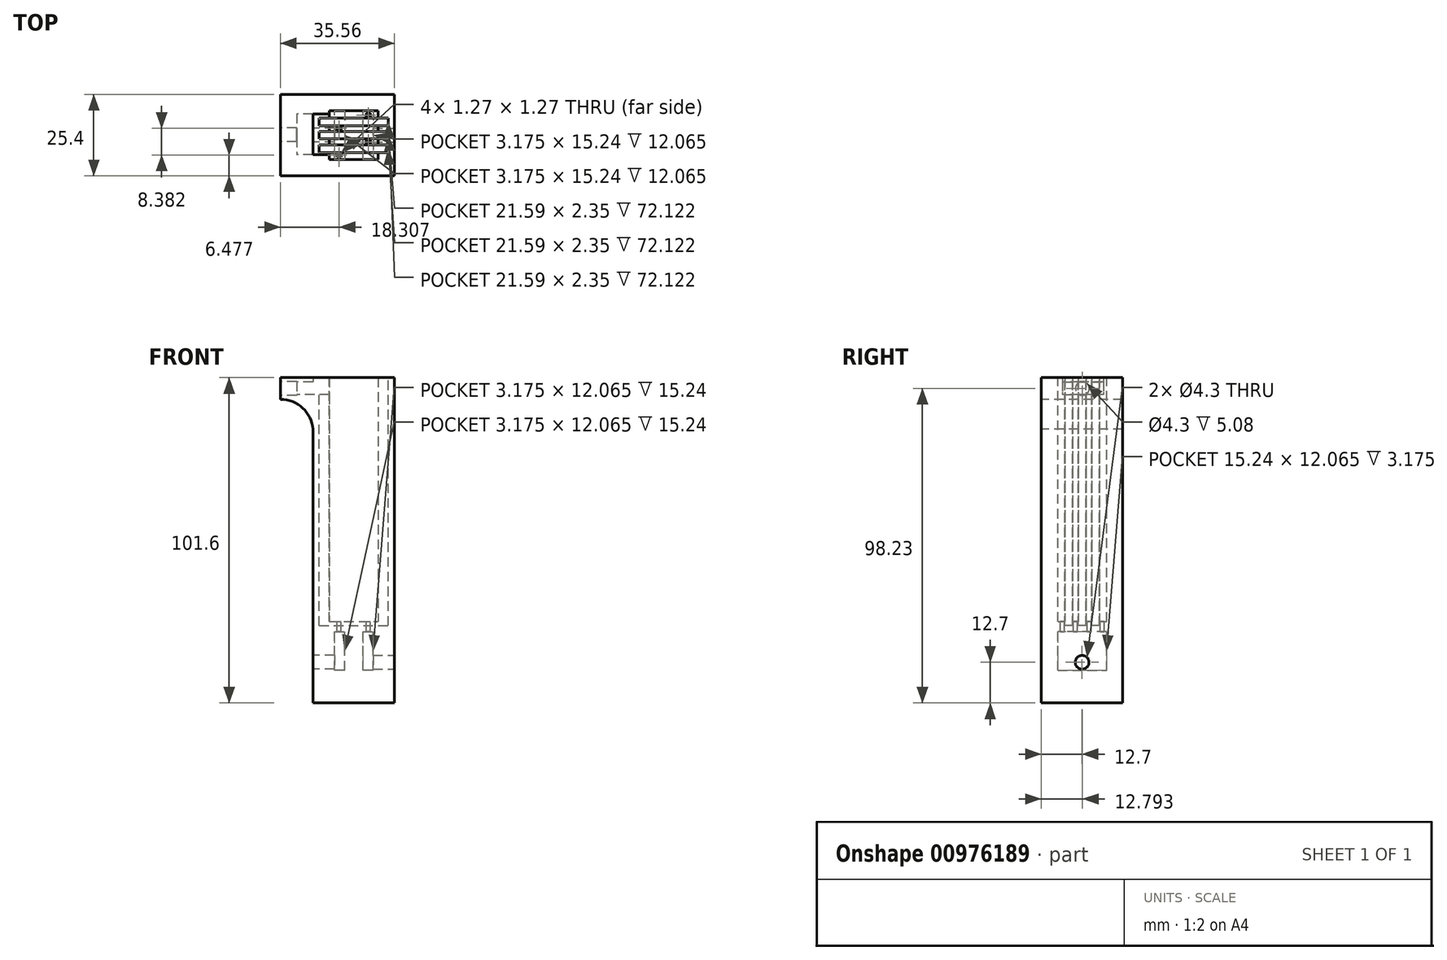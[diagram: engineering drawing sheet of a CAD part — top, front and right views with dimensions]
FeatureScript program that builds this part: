
annotation { "Feature Type Name" : "Feature", "Feature Type Description" : "" }
export const myFeature = defineFeature(function(context is Context, id is Id, definition is map)
    precondition{}
    {
        {
            var Q0;
            Q0=qCreatedBy(makeId("Top.planeOp"),FACE);
            var sketch = newSketch(context, id + "F0", { "sketchPlane" : qUnion([Q0])});
            skLineSegment(sketch, "E0.bottom", {"start": v(0, 0) * mm, "end": v(25.4, 0) * mm});
            skLineSegment(sketch, "E0.top", {"start": v(0, 25.4) * mm, "end": v(25.4, 25.4) * mm});
            skLineSegment(sketch, "E0.left", {"start": v(0, 0) * mm, "end": v(0, 25.4) * mm});
            skLineSegment(sketch, "E0.right", {"start": v(25.4, 0) * mm, "end": v(25.4, 25.4) * mm});
            skSolve(sketch);
        }
        {
            var Q0;
            Q0=makeQuery(id+"F0.imprint","IMPRINT",FACE,{"disambiguationData":[TD([[makeQuery(id+"F0.imprint","IMPRINT",EDGE,{"derivedFrom":sQuery(id+"F0.wireOp",EDGE,"E0.bottom")}),1.0]])]});
            extrude(context, id + "F1", {"entities" : qUnion([Q0]), "depth" : 101.6 * mm, "offsetDistance" : 25.4 * mm});
        }
        {
            var Q0;
            Q0=makeQuery(id+"F1.opExtrude","CAP_FACE",FACE,{"disambiguationData":[OSD([sQuery(id+"F0.wireOp",EDGE,"E0.bottom"),sQuery(id+"F0.wireOp",EDGE,"E0.top"),sQuery(id+"F0.wireOp",EDGE,"E0.left"),sQuery(id+"F0.wireOp",EDGE,"E0.right")])],"isStart":false});
            var sketch = newSketch(context, id + "F2", { "sketchPlane" : qUnion([Q0])});
            skLineSegment(sketch, "E1.bottom", {"start": v(5.08, 5.08) * mm, "end": v(20.32, 5.08) * mm});
            skLineSegment(sketch, "E1.top", {"start": v(5.08, 20.32) * mm, "end": v(20.32, 20.32) * mm});
            skLineSegment(sketch, "E1.left", {"start": v(5.08, 5.08) * mm, "end": v(5.08, 20.32) * mm});
            skLineSegment(sketch, "E1.right", {"start": v(20.32, 5.08) * mm, "end": v(20.32, 20.32) * mm});
            skSolve(sketch);
        }
        {
            var Q0;
            Q0=makeQuery(id+"F2.imprint","IMPRINT",FACE,{"disambiguationData":[TD([[makeQuery(id+"F2.imprint","IMPRINT",EDGE,{"derivedFrom":sQuery(id+"F2.wireOp",EDGE,"E1.bottom")}),1.0]])]});
            extrude(context, id + "F3", {"entities" : qUnion([Q0]), "operationType" : NewBodyOperationType.REMOVE, "oppositeDirection" : true, "depth" : 76.2 * mm, "offsetDistance" : 25.4 * mm});
        }
        {
            var Q0;
            Q0=makeQuery(id+"F1.opExtrude","SWEPT_FACE",FACE,{"disambiguationData":[OSD([sQuery(id+"F0.wireOp",EDGE,"E0.right")])]});
            var sketch = newSketch(context, id + "F4", { "sketchPlane" : qUnion([Q0])});
            skCircle(sketch, "E2", {"center": v(12.7, 12.7) * mm, "radius": 2.15 * mm});
            skSolve(sketch);
        }
        {
            var Q0;
            Q0=makeQuery(id+"F3.boolean.opBoolean","COPY",FACE,{"derivedFrom":makeQuery(id+"F3.opExtrude","CAP_FACE",FACE,{"disambiguationData":[OSD([sQuery(id+"F2.wireOp",EDGE,"E1.bottom"),sQuery(id+"F2.wireOp",EDGE,"E1.top"),sQuery(id+"F2.wireOp",EDGE,"E1.left"),sQuery(id+"F2.wireOp",EDGE,"E1.right")])],"isStart":false})});
            var sketch = newSketch(context, id + "F5", { "sketchPlane" : qUnion([Q0])});
            skLineSegment(sketch, "E3.bottom", {"start": v(15.56, 20.32) * mm, "end": v(18.73, 20.32) * mm});
            skLineSegment(sketch, "E3.top", {"start": v(15.56, 5.08) * mm, "end": v(18.73, 5.08) * mm});
            skLineSegment(sketch, "E3.left", {"start": v(15.56, 20.32) * mm, "end": v(15.56, 5.08) * mm});
            skLineSegment(sketch, "E3.right", {"start": v(18.73, 20.32) * mm, "end": v(18.73, 5.08) * mm});
            skLineSegment(sketch, "E4.bottom", {"start": v(6.67, 20.32) * mm, "end": v(9.84, 20.32) * mm});
            skLineSegment(sketch, "E4.top", {"start": v(6.67, 5.08) * mm, "end": v(9.84, 5.08) * mm});
            skLineSegment(sketch, "E4.left", {"start": v(6.67, 20.32) * mm, "end": v(6.67, 5.08) * mm});
            skLineSegment(sketch, "E4.right", {"start": v(9.84, 20.32) * mm, "end": v(9.84, 5.08) * mm});
            skSolve(sketch);
        }
        {
            var Q0;
            Q0=qSketchRegion(id+"F5",true);
            extrude(context, id + "F6", {"entities" : qUnion([Q0]), "operationType" : NewBodyOperationType.REMOVE, "endBound" : BoundingType.UP_TO_NEXT, "oppositeDirection" : true, "depth" : 25.4 * mm, "hasOffset" : true, "offsetDistance" : 10.16 * mm, "hasSecondDirection" : true, "secondDirectionOppositeDirection" : false, "secondDirectionDepth" : -3.17 * mm});
        }
        {
            var Q0;
            Q0=qSketchRegion(id+"F4",true);
            extrude(context, id + "F7", {"entities" : qUnion([Q0]), "operationType" : NewBodyOperationType.REMOVE, "endBound" : BoundingType.UP_TO_NEXT, "oppositeDirection" : true, "depth" : 25.4 * mm, "offsetDistance" : 25.4 * mm});
        }
        {
            var Q0;
            Q0=makeQuery(id+"F1.opExtrude","SWEPT_FACE",FACE,{"disambiguationData":[OSD([sQuery(id+"F0.wireOp",EDGE,"E0.left")])]});
            var sketch = newSketch(context, id + "F8", { "sketchPlane" : qUnion([Q0])});
            skCircle(sketch, "E5", {"center": v(-12.7, 12.7) * mm, "radius": 2.15 * mm});
            skSolve(sketch);
        }
        {
            var Q0;
            Q0=qSketchRegion(id+"F8",true);
            extrude(context, id + "F9", {"entities" : qUnion([Q0]), "operationType" : NewBodyOperationType.REMOVE, "endBound" : BoundingType.UP_TO_NEXT, "oppositeDirection" : true, "depth" : 25.4 * mm, "offsetDistance" : 25.4 * mm});
        }
        {
            var Q0;
            Q0=makeQuery(id+"F3.boolean.opBoolean","COPY",FACE,{"derivedFrom":makeQuery(id+"F3.opExtrude","CAP_FACE",FACE,{"disambiguationData":[OSD([sQuery(id+"F2.wireOp",EDGE,"E1.bottom"),sQuery(id+"F2.wireOp",EDGE,"E1.top"),sQuery(id+"F2.wireOp",EDGE,"E1.left"),sQuery(id+"F2.wireOp",EDGE,"E1.right")])],"isStart":false})});
            var sketch = newSketch(context, id + "F10", { "sketchPlane" : qUnion([Q0])});
            skLineSegment(sketch, "E6.bottom", {"start": v(16.57, 19.56) * mm, "end": v(17.84, 19.56) * mm});
            skLineSegment(sketch, "E6.top", {"start": v(16.57, 18.29) * mm, "end": v(17.84, 18.29) * mm});
            skLineSegment(sketch, "E6.left", {"start": v(16.57, 19.56) * mm, "end": v(16.57, 18.29) * mm});
            skLineSegment(sketch, "E6.right", {"start": v(17.84, 19.56) * mm, "end": v(17.84, 18.29) * mm});
            skLineSegment(sketch, "E7.0.1.0", {"start": v(16.57, 11.18) * mm, "end": v(17.84, 11.18) * mm});
            skLineSegment(sketch, "E7.0.1.1", {"start": v(17.84, 11.18) * mm, "end": v(17.84, 9.9) * mm});
            skLineSegment(sketch, "E7.0.1.2", {"start": v(16.57, 9.9) * mm, "end": v(17.84, 9.9) * mm});
            skLineSegment(sketch, "E7.0.1.3", {"start": v(16.57, 11.18) * mm, "end": v(16.57, 9.9) * mm});
            skLineSegment(sketch, "E7.direction1", {"start": v(16.57, 18.29) * mm, "end": v(41.97, 18.29) * mm, "construction": true});
            skLineSegment(sketch, "E7.direction2", {"start": v(16.57, 18.29) * mm, "end": v(16.57, 9.9) * mm, "construction": true});
            skSolve(sketch);
        }
        {
            var Q0;
            Q0=makeQuery(id+"F10.imprint","IMPRINT",FACE,{"disambiguationData":[TD([[makeQuery(id+"F10.imprint","IMPRINT",EDGE,{"derivedFrom":sQuery(id+"F10.wireOp",EDGE,"E6.bottom")}),1.0]])]});
            var sketch = newSketch(context, id + "F11", { "sketchPlane" : qUnion([Q0])});
            skLineSegment(sketch, "E8.bottom", {"start": v(7.51, 7.11) * mm, "end": v(8.78, 7.11) * mm});
            skLineSegment(sketch, "E8.top", {"start": v(7.51, 5.84) * mm, "end": v(8.78, 5.84) * mm});
            skLineSegment(sketch, "E8.left", {"start": v(7.51, 7.11) * mm, "end": v(7.51, 5.84) * mm});
            skLineSegment(sketch, "E8.right", {"start": v(8.78, 7.11) * mm, "end": v(8.78, 5.84) * mm});
            skLineSegment(sketch, "E9.bottom", {"start": v(7.51, 15.5) * mm, "end": v(8.78, 15.5) * mm});
            skLineSegment(sketch, "E9.top", {"start": v(7.51, 14.22) * mm, "end": v(8.78, 14.22) * mm});
            skLineSegment(sketch, "E9.left", {"start": v(7.51, 15.5) * mm, "end": v(7.51, 14.22) * mm});
            skLineSegment(sketch, "E9.right", {"start": v(8.78, 15.5) * mm, "end": v(8.78, 14.22) * mm});
            skSolve(sketch);
        }
        {
            var Q0;
            Q0=qSketchRegion(id+"F10",true);
            extrude(context, id + "F12", {"entities" : qUnion([Q0]), "operationType" : NewBodyOperationType.REMOVE, "endBound" : BoundingType.UP_TO_NEXT, "oppositeDirection" : true, "depth" : 25.4 * mm, "offsetDistance" : 25.4 * mm});
        }
        {
            var Q0;
            Q0=qSketchRegion(id+"F11",true);
            extrude(context, id + "F13", {"entities" : qUnion([Q0]), "operationType" : NewBodyOperationType.REMOVE, "endBound" : BoundingType.UP_TO_NEXT, "oppositeDirection" : true, "depth" : 25.4 * mm, "offsetDistance" : 25.4 * mm});
        }
        {
            var Q0;
            Q0=makeQuery(id+"F1.opExtrude","SWEPT_FACE",FACE,{"disambiguationData":[OSD([sQuery(id+"F0.wireOp",EDGE,"E0.left")])]});
            var sketch = newSketch(context, id + "F14", { "sketchPlane" : qUnion([Q0])});
            skLineSegment(sketch, "E10.bottom", {"start": v(-19.33, 100.27) * mm, "end": v(-6.55, 100.27) * mm});
            skLineSegment(sketch, "E10.top", {"start": v(-19.33, 96.25) * mm, "end": v(-6.55, 96.25) * mm});
            skLineSegment(sketch, "E10.left", {"start": v(-19.33, 100.27) * mm, "end": v(-19.33, 96.25) * mm});
            skLineSegment(sketch, "E10.right", {"start": v(-6.55, 100.27) * mm, "end": v(-6.55, 96.25) * mm});
            skSolve(sketch);
        }
        {
            var Q0;
            Q0=qSketchRegion(id+"F14",true);
            extrude(context, id + "F15", {"entities" : qUnion([Q0]), "operationType" : NewBodyOperationType.REMOVE, "endBound" : BoundingType.UP_TO_NEXT, "oppositeDirection" : true, "depth" : 25.4 * mm, "offsetDistance" : 25.4 * mm});
        }
        {
            var Q0;
            Q0=makeQuery(id+"F1.opExtrude","SWEPT_FACE",FACE,{"disambiguationData":[OSD([sQuery(id+"F0.wireOp",EDGE,"E0.left")])]});
            var sketch = newSketch(context, id + "F16", { "sketchPlane" : qUnion([Q0])});
            skLineSegment(sketch, "E11.bottom", {"start": v(-25.4, 101.6) * mm, "end": v(0, 101.6) * mm});
            skLineSegment(sketch, "E11.top", {"start": v(-25.4, 94.82) * mm, "end": v(0, 94.82) * mm});
            skLineSegment(sketch, "E11.left", {"start": v(-25.4, 101.6) * mm, "end": v(-25.4, 94.82) * mm});
            skLineSegment(sketch, "E11.right", {"start": v(0, 101.6) * mm, "end": v(0, 94.82) * mm});
            skSolve(sketch);
        }
        {
            var Q0;
            Q0=makeQuery(id+"F16.imprint","IMPRINT",FACE,{"disambiguationData":[TD([[makeQuery(id+"F16.imprint","IMPRINT",EDGE,{"derivedFrom":sQuery(id+"F16.wireOp",EDGE,"E11.bottom")}),1.0]])]});
            extrude(context, id + "F17", {"entities" : qUnion([Q0]), "operationType" : NewBodyOperationType.ADD, "depth" : 5.08 * mm, "offsetDistance" : 25.4 * mm});
        }
        {
            var Q0;
            Q0=makeQuery(id+"F17.opExtrude","CAP_FACE",FACE,{"disambiguationData":[OSD([sQuery(id+"F14.wireOp",EDGE,"E10.bottom"),sQuery(id+"F14.wireOp",EDGE,"E10.top"),sQuery(id+"F14.wireOp",EDGE,"E10.left"),sQuery(id+"F14.wireOp",EDGE,"E10.right"),sQuery(id+"F16.wireOp",EDGE,"E11.bottom"),sQuery(id+"F16.wireOp",EDGE,"E11.top"),sQuery(id+"F16.wireOp",EDGE,"E11.left"),sQuery(id+"F16.wireOp",EDGE,"E11.right")])],"isStart":false});
            var sketch = newSketch(context, id + "F18", { "sketchPlane" : qUnion([Q0])});
            skLineSegment(sketch, "E12.bottom", {"start": v(-25.4, 101.6) * mm, "end": v(0, 101.6) * mm});
            skLineSegment(sketch, "E12.top", {"start": v(-25.4, 94.82) * mm, "end": v(0, 94.82) * mm});
            skLineSegment(sketch, "E12.left", {"start": v(-25.4, 101.6) * mm, "end": v(-25.4, 94.82) * mm});
            skLineSegment(sketch, "E12.right", {"start": v(0, 101.6) * mm, "end": v(0, 94.82) * mm});
            skSolve(sketch);
        }
        {
            var Q0;
            Q0=qSketchRegion(id+"F18",true);
            extrude(context, id + "F19", {"entities" : qUnion([Q0]), "operationType" : NewBodyOperationType.ADD, "depth" : 5.08 * mm, "offsetDistance" : 25.4 * mm});
        }
        {
            var Q0;
            Q0=makeQuery(id+"F19.opExtrude","CAP_FACE",FACE,{"disambiguationData":[OSD([sQuery(id+"F18.wireOp",EDGE,"E12.bottom"),sQuery(id+"F18.wireOp",EDGE,"E12.top"),sQuery(id+"F18.wireOp",EDGE,"E12.left"),sQuery(id+"F18.wireOp",EDGE,"E12.right")])],"isStart":false});
            var sketch = newSketch(context, id + "F20", { "sketchPlane" : qUnion([Q0])});
            skCircle(sketch, "E13", {"center": v(-12.8, 98.23) * mm, "radius": 2.15 * mm});
            skSolve(sketch);
        }
        {
            var Q0;
            Q0=qSketchRegion(id+"F20",true);
            extrude(context, id + "F21", {"entities" : qUnion([Q0]), "operationType" : NewBodyOperationType.REMOVE, "oppositeDirection" : true, "depth" : 5.08 * mm, "offsetDistance" : 25.4 * mm});
        }
        {
            var Q0;
            Q0=makeQuery(id+"F19.boolean.opBoolean","MERGE",FACE,{"derivedFrom":[makeQuery(id+"F17.boolean.opBoolean","MERGE",FACE,{"derivedFrom":[makeQuery(id+"F1.opExtrude","SWEPT_FACE",FACE,{"disambiguationData":[OSD([sQuery(id+"F0.wireOp",EDGE,"E0.bottom")])]}),makeQuery(id+"F17.opExtrude","SWEPT_FACE",FACE,{"disambiguationData":[OSD([sQuery(id+"F16.wireOp",EDGE,"E11.right")])]})]}),makeQuery(id+"F19.opExtrude","SWEPT_FACE",FACE,{"disambiguationData":[OSD([sQuery(id+"F18.wireOp",EDGE,"E12.right")])]})]});
            var sketch = newSketch(context, id + "F22", { "sketchPlane" : qUnion([Q0])});
            skArc(sketch, "E14", {"start": v(0, 85.44) * mm, "mid": v(-3.25, 92.12) * mm, "end": v(-10.16, 94.82) * mm});
            skLineSegment(sketch, "E15", {"start": v(-10.16, 94.82) * mm, "end": v(0, 94.82) * mm});
            skLineSegment(sketch, "E16", {"start": v(0, 94.82) * mm, "end": v(0, 85.44) * mm});
            skSolve(sketch);
        }
        {
            var Q0;
            Q0=qSketchRegion(id+"F22",true);
            var Q1;
            Q1=makeQuery(id+"F19.boolean.opBoolean","MERGE",FACE,{"derivedFrom":[makeQuery(id+"F17.boolean.opBoolean","MERGE",FACE,{"derivedFrom":[makeQuery(id+"F1.opExtrude","SWEPT_FACE",FACE,{"disambiguationData":[OSD([sQuery(id+"F0.wireOp",EDGE,"E0.top")])]}),makeQuery(id+"F17.opExtrude","SWEPT_FACE",FACE,{"disambiguationData":[OSD([sQuery(id+"F16.wireOp",EDGE,"E11.left")])]})]}),makeQuery(id+"F19.opExtrude","SWEPT_FACE",FACE,{"disambiguationData":[OSD([sQuery(id+"F18.wireOp",EDGE,"E12.left")])]})]});
            extrude(context, id + "F23", {"entities" : qUnion([Q0]), "operationType" : NewBodyOperationType.ADD, "endBound" : BoundingType.UP_TO_SURFACE, "oppositeDirection" : true, "depth" : 25.4 * mm, "endBoundEntityFace" : qUnion([Q1]), "offsetDistance" : 25.4 * mm});
        }
        {
            var Q0;
            Q0=makeQuery(id+"F19.boolean.opBoolean","MERGE",FACE,{"derivedFrom":[makeQuery(id+"F17.boolean.opBoolean","MERGE",FACE,{"derivedFrom":[makeQuery(id+"F1.opExtrude","CAP_FACE",FACE,{"disambiguationData":[OSD([sQuery(id+"F0.wireOp",EDGE,"E0.bottom"),sQuery(id+"F0.wireOp",EDGE,"E0.top"),sQuery(id+"F0.wireOp",EDGE,"E0.left"),sQuery(id+"F0.wireOp",EDGE,"E0.right")])],"isStart":false}),makeQuery(id+"F17.opExtrude","SWEPT_FACE",FACE,{"disambiguationData":[OSD([sQuery(id+"F16.wireOp",EDGE,"E11.bottom")])]})]}),makeQuery(id+"F19.opExtrude","SWEPT_FACE",FACE,{"disambiguationData":[OSD([sQuery(id+"F18.wireOp",EDGE,"E12.bottom")])]})]});
            var sketch = newSketch(context, id + "F24", { "sketchPlane" : qUnion([Q0])});
            skLineSegment(sketch, "E17.bottom", {"start": v(1.9, 18.03) * mm, "end": v(23.5, 18.03) * mm});
            skLineSegment(sketch, "E17.top", {"start": v(1.9, 15.68) * mm, "end": v(23.5, 15.68) * mm});
            skLineSegment(sketch, "E17.left", {"start": v(1.9, 18.03) * mm, "end": v(1.9, 15.68) * mm});
            skLineSegment(sketch, "E17.right", {"start": v(23.5, 18.03) * mm, "end": v(23.5, 15.68) * mm});
            skLineSegment(sketch, "E18.bottom", {"start": v(1.9, 9.65) * mm, "end": v(23.5, 9.65) * mm});
            skLineSegment(sketch, "E18.top", {"start": v(1.9, 7.3) * mm, "end": v(23.5, 7.3) * mm});
            skLineSegment(sketch, "E18.left", {"start": v(1.9, 9.65) * mm, "end": v(1.9, 7.3) * mm});
            skLineSegment(sketch, "E18.right", {"start": v(23.5, 9.65) * mm, "end": v(23.5, 7.3) * mm});
            skLineSegment(sketch, "E19.bottom", {"start": v(1.9, 13.9) * mm, "end": v(23.5, 13.9) * mm});
            skLineSegment(sketch, "E19.top", {"start": v(1.9, 11.56) * mm, "end": v(23.5, 11.56) * mm});
            skLineSegment(sketch, "E19.left", {"start": v(1.9, 13.9) * mm, "end": v(1.9, 11.56) * mm});
            skLineSegment(sketch, "E19.right", {"start": v(23.5, 13.9) * mm, "end": v(23.5, 11.56) * mm});
            skSolve(sketch);
        }
        {
            var Q0;
            Q0=qSketchRegion(id+"F24",true);
            extrude(context, id + "F25", {"entities" : qUnion([Q0]), "operationType" : NewBodyOperationType.REMOVE, "oppositeDirection" : true, "depth" : 77.47 * mm, "offsetDistance" : 25.4 * mm});
        }
        {
            var Q0;
            {var subQ0=sQuery(id+"F14.wireOp",EDGE,"E10.bottom");Q0=makeQuery(id+"F25.boolean.opBoolean","SPLIT",FACE,{"disambiguationData":[TD([makeQuery(id+"F1.opExtrude","CAP_FACE",FACE,{"disambiguationData":[OSD([sQuery(id+"F0.wireOp",EDGE,"E0.bottom"),sQuery(id+"F0.wireOp",EDGE,"E0.top"),sQuery(id+"F0.wireOp",EDGE,"E0.left"),sQuery(id+"F0.wireOp",EDGE,"E0.right")])],"isStart":false}),makeQuery(id+"F15.boolean.opBoolean","COPY",FACE,{"derivedFrom":makeQuery(id+"F15.opExtrude","SWEPT_FACE",FACE,{"disambiguationData":[OSD([subQ0])]})}),makeQuery(id+"F17.opExtrude","SWEPT_FACE",FACE,{"disambiguationData":[OSD([sQuery(id+"F16.wireOp",EDGE,"E11.bottom")])]}),makeQuery(id+"F17.opExtrude","SWEPT_FACE",FACE,{"disambiguationData":[OSD([subQ0])]}),makeQuery(id+"F19.opExtrude","SWEPT_FACE",FACE,{"disambiguationData":[OSD([sQuery(id+"F18.wireOp",EDGE,"E12.bottom")])]}),makeQuery(id+"F25.opExtrude","SWEPT_FACE",FACE,{"disambiguationData":[OSD([sQuery(id+"F24.wireOp",EDGE,"E18.top")])]}),makeQuery(id+"F25.opExtrude","SWEPT_FACE",FACE,{"disambiguationData":[OSD([sQuery(id+"F24.wireOp",EDGE,"932b69c3-4fd8-45e5-8434-84e7324a444d.bottom")])]})])],"derivedFrom":makeQuery(id+"F3.boolean.opBoolean","COPY",FACE,{"derivedFrom":makeQuery(id+"F3.opExtrude","SWEPT_FACE",FACE,{"disambiguationData":[OSD([sQuery(id+"F2.wireOp",EDGE,"E1.left")])]})})});}
            var sketch = newSketch(context, id + "F26", { "sketchPlane" : qUnion([Q0])});
            skLineSegment(sketch, "E20.bottom", {"start": v(6.55, 101.6) * mm, "end": v(19.33, 101.6) * mm});
            skLineSegment(sketch, "E20.top", {"start": v(6.55, 100.27) * mm, "end": v(19.33, 100.27) * mm});
            skLineSegment(sketch, "E20.left", {"start": v(6.55, 101.6) * mm, "end": v(6.55, 100.27) * mm});
            skLineSegment(sketch, "E20.right", {"start": v(19.33, 101.6) * mm, "end": v(19.33, 100.27) * mm});
            skSolve(sketch);
        }
        {
            var Q0;
            Q0=qSketchRegion(id+"F26",true);
            var Q1;
            {var subQ0=sQuery(id+"F14.wireOp",EDGE,"E10.bottom");Q1=makeQuery(id+"F25.boolean.opBoolean","COPY",FACE,{"disambiguationData":[TD([makeQuery(id+"F15.boolean.opBoolean","COPY",FACE,{"derivedFrom":makeQuery(id+"F15.opExtrude","SWEPT_FACE",FACE,{"disambiguationData":[OSD([subQ0])]})})])],"derivedFrom":makeQuery(id+"F25.opExtrude","SWEPT_FACE",FACE,{"disambiguationData":[OSD([sQuery(id+"F24.wireOp",EDGE,"E18.left")])]})});}
            extrude(context, id + "F27", {"entities" : qUnion([Q0]), "operationType" : NewBodyOperationType.REMOVE, "oppositeDirection" : true, "depth" : 5.08 * mm, "endBoundEntityFace" : qUnion([Q1]), "offsetDistance" : 25.4 * mm});
        }
    });
